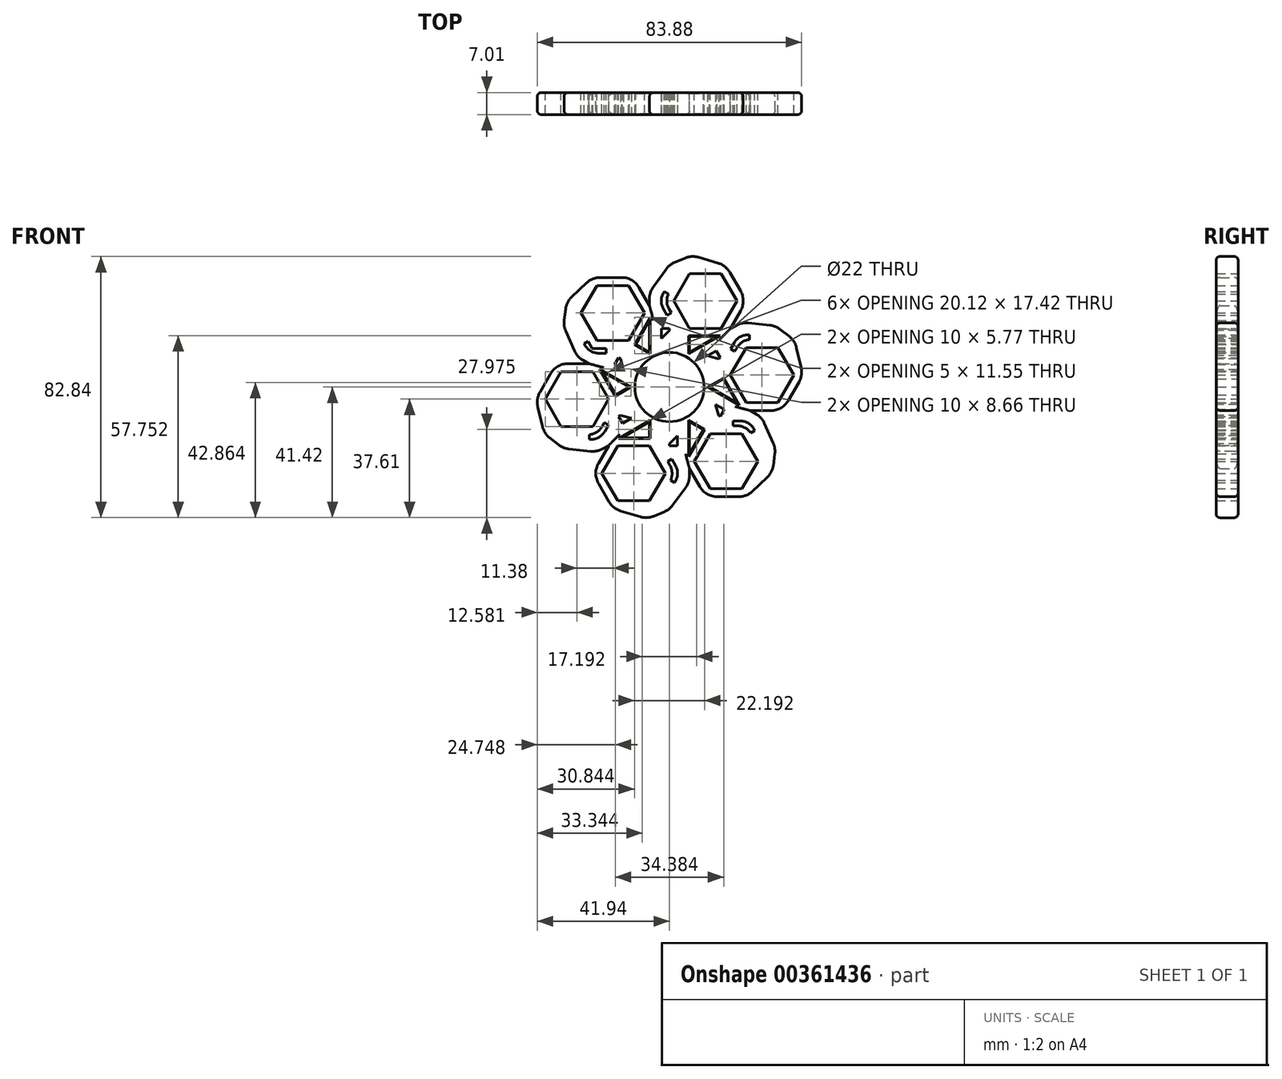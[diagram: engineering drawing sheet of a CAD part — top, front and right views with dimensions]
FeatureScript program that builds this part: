
annotation { "Feature Type Name" : "Feature", "Feature Type Description" : "" }
export const myFeature = defineFeature(function(context is Context, id is Id, definition is map)
    precondition{}
    {
        {
            var Q0;
            Q0=qCreatedBy(makeId("Front.planeOp"),FACE);
            var sketch = newSketch(context, id + "F0", { "sketchPlane" : qUnion([Q0])});
            skCircle(sketch, "E0.cCircle", {"center": v(0, 0) * mm, "radius": 11 * mm, "construction": true});
            skLineSegment(sketch, "E0.0", {"start": v(6.35, -11) * mm, "end": v(-6.35, -11) * mm});
            skLineSegment(sketch, "E0.1", {"start": v(-6.35, -11) * mm, "end": v(-12.7, 0) * mm});
            skLineSegment(sketch, "E0.2", {"start": v(-12.7, 0) * mm, "end": v(-6.35, 11) * mm});
            skLineSegment(sketch, "E0.3", {"start": v(-6.35, 11) * mm, "end": v(6.35, 11) * mm});
            skLineSegment(sketch, "E0.4", {"start": v(6.35, 11) * mm, "end": v(12.7, 0) * mm});
            skLineSegment(sketch, "E0.5", {"start": v(12.7, 0) * mm, "end": v(6.35, -11) * mm});
            skPoint(sketch, "E0.0.midPoint", {"position": v(0, -11) * mm});
            skCircle(sketch, "E1.cCircle", {"center": v(11.38, 27.33) * mm, "radius": 8.71 * mm, "construction": true});
            skLineSegment(sketch, "E1.0", {"start": v(16.4, 18.62) * mm, "end": v(6.35, 18.62) * mm});
            skLineSegment(sketch, "E1.1", {"start": v(6.35, 18.62) * mm, "end": v(1.32, 27.33) * mm});
            skLineSegment(sketch, "E1.2", {"start": v(1.32, 27.33) * mm, "end": v(6.35, 36.04) * mm});
            skLineSegment(sketch, "E1.3", {"start": v(6.35, 36.04) * mm, "end": v(16.4, 36.04) * mm});
            skLineSegment(sketch, "E1.4", {"start": v(16.4, 36.04) * mm, "end": v(21.44, 27.33) * mm});
            skLineSegment(sketch, "E1.5", {"start": v(21.44, 27.33) * mm, "end": v(16.4, 18.62) * mm});
            skPoint(sketch, "E1.0.midPoint", {"position": v(11.38, 18.62) * mm});
            skLineSegment(sketch, "E2", {"start": v(6.35, 11) * mm, "end": v(6.35, 18.62) * mm});
            skLineSegment(sketch, "E3", {"start": v(-6.35, 11) * mm, "end": v(-6.35, 30.15) * mm});
            skLineSegment(sketch, "E4", {"start": v(0, 38.86) * mm, "end": v(-6.35, 30.15) * mm});
            skLineSegment(sketch, "E5", {"start": v(7.1, 41.8) * mm, "end": v(0, 38.86) * mm});
            skLineSegment(sketch, "E6.0", {"start": v(-1.61, 27.33) * mm, "end": v(4.88, 38.58) * mm});
            skLineSegment(sketch, "E6.1", {"start": v(17.88, 38.58) * mm, "end": v(24.37, 27.33) * mm});
            skLineSegment(sketch, "E6.2", {"start": v(24.37, 27.33) * mm, "end": v(17.88, 16.08) * mm});
            skLineSegment(sketch, "E6.3", {"start": v(4.88, 38.58) * mm, "end": v(17.88, 38.58) * mm});
            skLineSegment(sketch, "E6.4", {"start": v(17.88, 16.08) * mm, "end": v(4.88, 16.08) * mm});
            skLineSegment(sketch, "E6.5", {"start": v(4.88, 16.08) * mm, "end": v(-1.61, 27.33) * mm});
            skLineSegment(sketch, "E7", {"start": v(17.88, 38.58) * mm, "end": v(7.1, 41.8) * mm});
            skLineSegment(sketch, "E8.1.0", {"start": v(-32.65, 27.06) * mm, "end": v(-33.65, 19.43) * mm});
            skLineSegment(sketch, "E8.1.1", {"start": v(-24.48, 34.77) * mm, "end": v(-32.65, 27.06) * mm});
            skLineSegment(sketch, "E8.1.2", {"start": v(-24.48, 34.77) * mm, "end": v(-11.48, 34.77) * mm});
            skLineSegment(sketch, "E8.1.3", {"start": v(-11.48, 34.77) * mm, "end": v(-4.99, 23.52) * mm});
            skLineSegment(sketch, "E8.1.4", {"start": v(-4.99, 23.52) * mm, "end": v(-11.48, 12.27) * mm});
            skLineSegment(sketch, "E8.1.5", {"start": v(-11.48, 12.27) * mm, "end": v(-24.48, 12.27) * mm});
            skLineSegment(sketch, "E8.1.6", {"start": v(-24.48, 12.27) * mm, "end": v(-30.97, 23.52) * mm});
            skLineSegment(sketch, "E8.1.7", {"start": v(-23, 14.8) * mm, "end": v(-28.04, 23.52) * mm});
            skCircle(sketch, "E8.1.8", {"center": v(-17.98, 23.52) * mm, "radius": 8.71 * mm, "construction": true});
            skLineSegment(sketch, "E8.1.9", {"start": v(-33.65, 19.43) * mm, "end": v(-29.28, 9.57) * mm});
            skLineSegment(sketch, "E8.1.10", {"start": v(-23, 32.23) * mm, "end": v(-12.95, 32.23) * mm});
            skLineSegment(sketch, "E8.1.11", {"start": v(-12.7, 0) * mm, "end": v(-29.28, 9.57) * mm});
            skPoint(sketch, "E8.1.12", {"position": v(-10.43, 19.16) * mm});
            skLineSegment(sketch, "E8.1.13", {"start": v(-12.95, 32.23) * mm, "end": v(-7.92, 23.52) * mm});
            skLineSegment(sketch, "E8.1.14", {"start": v(-30.97, 23.52) * mm, "end": v(-24.48, 34.77) * mm});
            skLineSegment(sketch, "E8.1.15", {"start": v(-12.95, 14.8) * mm, "end": v(-23, 14.8) * mm});
            skLineSegment(sketch, "E8.1.16", {"start": v(-7.92, 23.52) * mm, "end": v(-12.95, 14.8) * mm});
            skLineSegment(sketch, "E8.1.17", {"start": v(-28.04, 23.52) * mm, "end": v(-23, 32.23) * mm});
            skLineSegment(sketch, "E8.1.18", {"start": v(-6.35, 11) * mm, "end": v(-12.95, 14.8) * mm});
            skLineSegment(sketch, "E8.2.0", {"start": v(-39.76, -14.75) * mm, "end": v(-33.65, -19.43) * mm});
            skLineSegment(sketch, "E8.2.1", {"start": v(-42.35, -3.81) * mm, "end": v(-39.76, -14.75) * mm});
            skLineSegment(sketch, "E8.2.2", {"start": v(-42.35, -3.8) * mm, "end": v(-35.86, 7.44) * mm});
            skLineSegment(sketch, "E8.2.3", {"start": v(-35.86, 7.44) * mm, "end": v(-22.86, 7.44) * mm});
            skLineSegment(sketch, "E8.2.4", {"start": v(-22.86, 7.44) * mm, "end": v(-16.37, -3.81) * mm});
            skLineSegment(sketch, "E8.2.5", {"start": v(-16.37, -3.8) * mm, "end": v(-22.86, -15.06) * mm});
            skLineSegment(sketch, "E8.2.6", {"start": v(-22.86, -15.06) * mm, "end": v(-35.86, -15.06) * mm});
            skLineSegment(sketch, "E8.2.7", {"start": v(-24.33, -12.52) * mm, "end": v(-34.39, -12.52) * mm});
            skCircle(sketch, "E8.2.8", {"center": v(-29.36, -3.81) * mm, "radius": 8.71 * mm, "construction": true});
            skLineSegment(sketch, "E8.2.9", {"start": v(-33.65, -19.43) * mm, "end": v(-22.93, -20.57) * mm});
            skLineSegment(sketch, "E8.2.10", {"start": v(-39.42, -3.81) * mm, "end": v(-34.39, 4.9) * mm});
            skLineSegment(sketch, "E8.2.11", {"start": v(-6.35, -11) * mm, "end": v(-22.93, -20.57) * mm});
            skPoint(sketch, "E8.2.12", {"position": v(-21.81, 0.55) * mm});
            skLineSegment(sketch, "E8.2.13", {"start": v(-34.39, 4.9) * mm, "end": v(-24.33, 4.9) * mm});
            skLineSegment(sketch, "E8.2.14", {"start": v(-35.86, -15.06) * mm, "end": v(-42.35, -3.81) * mm});
            skLineSegment(sketch, "E8.2.15", {"start": v(-19.3, -3.81) * mm, "end": v(-24.33, -12.52) * mm});
            skLineSegment(sketch, "E8.2.16", {"start": v(-24.33, 4.9) * mm, "end": v(-19.3, -3.81) * mm});
            skLineSegment(sketch, "E8.2.17", {"start": v(-34.39, -12.52) * mm, "end": v(-39.42, -3.81) * mm});
            skLineSegment(sketch, "E8.2.18", {"start": v(-12.7, 0) * mm, "end": v(-19.3, -3.81) * mm});
            skLineSegment(sketch, "E9.2.3.0", {"start": v(-7.1, -41.8) * mm, "end": v(0, -38.86) * mm});
            skLineSegment(sketch, "E9.3.3.0", {"start": v(-17.88, -38.58) * mm, "end": v(-7.1, -41.8) * mm});
            skLineSegment(sketch, "E9.6.3.0", {"start": v(-17.88, -38.58) * mm, "end": v(-24.37, -27.33) * mm});
            skLineSegment(sketch, "E9.9.3.0", {"start": v(-24.37, -27.33) * mm, "end": v(-17.88, -16.08) * mm});
            skLineSegment(sketch, "E9.12.3.0", {"start": v(-17.88, -16.08) * mm, "end": v(-4.88, -16.08) * mm});
            skLineSegment(sketch, "E9.15.3.0", {"start": v(-4.88, -16.08) * mm, "end": v(1.61, -27.33) * mm});
            skLineSegment(sketch, "E9.18.3.0", {"start": v(1.61, -27.33) * mm, "end": v(-4.88, -38.58) * mm});
            skLineSegment(sketch, "E9.21.3.0", {"start": v(-1.32, -27.33) * mm, "end": v(-6.35, -36.04) * mm});
            skCircle(sketch, "E9.24.3.0", {"center": v(-11.38, -27.33) * mm, "radius": 8.71 * mm, "construction": true});
            skLineSegment(sketch, "E9.26.3.0", {"start": v(0, -38.86) * mm, "end": v(6.35, -30.15) * mm});
            skLineSegment(sketch, "E9.29.3.0", {"start": v(-16.4, -36.04) * mm, "end": v(-21.44, -27.33) * mm});
            skLineSegment(sketch, "E9.32.3.0", {"start": v(6.35, -11) * mm, "end": v(6.35, -30.15) * mm});
            skPoint(sketch, "E9.35.3.0", {"position": v(-11.38, -18.62) * mm});
            skLineSegment(sketch, "E9.36.3.0", {"start": v(-21.44, -27.33) * mm, "end": v(-16.4, -18.62) * mm});
            skLineSegment(sketch, "E9.39.3.0", {"start": v(-4.88, -38.58) * mm, "end": v(-17.88, -38.58) * mm});
            skLineSegment(sketch, "E9.42.3.0", {"start": v(-6.35, -18.62) * mm, "end": v(-1.32, -27.33) * mm});
            skLineSegment(sketch, "E9.45.3.0", {"start": v(-16.4, -18.62) * mm, "end": v(-6.35, -18.62) * mm});
            skLineSegment(sketch, "E9.48.3.0", {"start": v(-6.35, -36.04) * mm, "end": v(-16.4, -36.04) * mm});
            skLineSegment(sketch, "E9.51.3.0", {"start": v(-6.35, -11) * mm, "end": v(-6.35, -18.62) * mm});
            skLineSegment(sketch, "E9.2.4.0", {"start": v(32.65, -27.06) * mm, "end": v(33.65, -19.43) * mm});
            skLineSegment(sketch, "E9.3.4.0", {"start": v(24.48, -34.77) * mm, "end": v(32.65, -27.06) * mm});
            skLineSegment(sketch, "E9.6.4.0", {"start": v(24.48, -34.77) * mm, "end": v(11.48, -34.77) * mm});
            skLineSegment(sketch, "E9.9.4.0", {"start": v(11.48, -34.77) * mm, "end": v(4.99, -23.52) * mm});
            skLineSegment(sketch, "E9.12.4.0", {"start": v(4.99, -23.52) * mm, "end": v(11.48, -12.27) * mm});
            skLineSegment(sketch, "E9.15.4.0", {"start": v(11.48, -12.27) * mm, "end": v(24.48, -12.27) * mm});
            skLineSegment(sketch, "E9.18.4.0", {"start": v(24.48, -12.27) * mm, "end": v(30.97, -23.52) * mm});
            skLineSegment(sketch, "E9.21.4.0", {"start": v(23, -14.8) * mm, "end": v(28.04, -23.52) * mm});
            skCircle(sketch, "E9.24.4.0", {"center": v(17.98, -23.52) * mm, "radius": 8.71 * mm, "construction": true});
            skLineSegment(sketch, "E9.26.4.0", {"start": v(33.65, -19.43) * mm, "end": v(29.28, -9.57) * mm});
            skLineSegment(sketch, "E9.29.4.0", {"start": v(23, -32.23) * mm, "end": v(12.95, -32.23) * mm});
            skLineSegment(sketch, "E9.32.4.0", {"start": v(12.7, 0) * mm, "end": v(29.28, -9.57) * mm});
            skPoint(sketch, "E9.35.4.0", {"position": v(10.43, -19.16) * mm});
            skLineSegment(sketch, "E9.36.4.0", {"start": v(12.95, -32.23) * mm, "end": v(7.92, -23.52) * mm});
            skLineSegment(sketch, "E9.39.4.0", {"start": v(30.97, -23.52) * mm, "end": v(24.48, -34.77) * mm});
            skLineSegment(sketch, "E9.42.4.0", {"start": v(12.95, -14.8) * mm, "end": v(23, -14.8) * mm});
            skLineSegment(sketch, "E9.45.4.0", {"start": v(7.92, -23.52) * mm, "end": v(12.95, -14.8) * mm});
            skLineSegment(sketch, "E9.48.4.0", {"start": v(28.04, -23.52) * mm, "end": v(23, -32.23) * mm});
            skLineSegment(sketch, "E9.51.4.0", {"start": v(6.35, -11) * mm, "end": v(12.95, -14.8) * mm});
            skLineSegment(sketch, "E9.2.5.0", {"start": v(39.76, 14.75) * mm, "end": v(33.65, 19.43) * mm});
            skLineSegment(sketch, "E9.3.5.0", {"start": v(42.35, 3.81) * mm, "end": v(39.76, 14.75) * mm});
            skLineSegment(sketch, "E9.6.5.0", {"start": v(42.35, 3.81) * mm, "end": v(35.86, -7.44) * mm});
            skLineSegment(sketch, "E9.9.5.0", {"start": v(35.86, -7.44) * mm, "end": v(22.86, -7.44) * mm});
            skLineSegment(sketch, "E9.12.5.0", {"start": v(22.86, -7.44) * mm, "end": v(16.37, 3.81) * mm});
            skLineSegment(sketch, "E9.15.5.0", {"start": v(16.37, 3.81) * mm, "end": v(22.86, 15.06) * mm});
            skLineSegment(sketch, "E9.18.5.0", {"start": v(22.86, 15.06) * mm, "end": v(35.86, 15.06) * mm});
            skLineSegment(sketch, "E9.21.5.0", {"start": v(24.33, 12.52) * mm, "end": v(34.39, 12.52) * mm});
            skCircle(sketch, "E9.24.5.0", {"center": v(29.36, 3.81) * mm, "radius": 8.71 * mm, "construction": true});
            skLineSegment(sketch, "E9.26.5.0", {"start": v(33.65, 19.43) * mm, "end": v(22.93, 20.57) * mm});
            skLineSegment(sketch, "E9.29.5.0", {"start": v(39.42, 3.8) * mm, "end": v(34.39, -4.9) * mm});
            skLineSegment(sketch, "E9.32.5.0", {"start": v(6.35, 11) * mm, "end": v(22.93, 20.57) * mm});
            skPoint(sketch, "E9.35.5.0", {"position": v(21.81, -0.55) * mm});
            skLineSegment(sketch, "E9.36.5.0", {"start": v(34.39, -4.9) * mm, "end": v(24.33, -4.9) * mm});
            skLineSegment(sketch, "E9.39.5.0", {"start": v(35.86, 15.06) * mm, "end": v(42.35, 3.81) * mm});
            skLineSegment(sketch, "E9.42.5.0", {"start": v(19.3, 3.81) * mm, "end": v(24.33, 12.52) * mm});
            skLineSegment(sketch, "E9.45.5.0", {"start": v(24.33, -4.9) * mm, "end": v(19.3, 3.81) * mm});
            skLineSegment(sketch, "E9.48.5.0", {"start": v(34.39, 12.52) * mm, "end": v(39.42, 3.81) * mm});
            skLineSegment(sketch, "E9.51.5.0", {"start": v(12.7, 0) * mm, "end": v(19.3, 3.81) * mm});
            skCircle(sketch, "E10", {"center": v(0, 0) * mm, "radius": 11 * mm});
            skLineSegment(sketch, "E11", {"start": v(0, 0) * mm, "end": v(0, 18.62) * mm});
            skLineSegment(sketch, "E12", {"start": v(0, 18.62) * mm, "end": v(-2.54, 18.62) * mm});
            skLineSegment(sketch, "E13", {"start": v(-2.54, 18.62) * mm, "end": v(-2.54, 13.54) * mm});
            skLineSegment(sketch, "E14", {"start": v(-2.54, 13.54) * mm, "end": v(0, 13.54) * mm});
            skPoint(sketch, "E14.endSnap0", {"position": v(0, 11) * mm});
            skLineSegment(sketch, "E15.1.0", {"start": v(-16.12, 9.3) * mm, "end": v(-17.4, 7.1) * mm});
            skLineSegment(sketch, "E15.1.1", {"start": v(-17.4, 7.1) * mm, "end": v(-13, 4.57) * mm});
            skLineSegment(sketch, "E15.1.2", {"start": v(-13, 4.57) * mm, "end": v(-11.72, 6.77) * mm});
            skLineSegment(sketch, "E15.1.3", {"start": v(0, 0) * mm, "end": v(-16.12, 9.3) * mm});
            skLineSegment(sketch, "E15.2.0", {"start": v(-16.12, -9.3) * mm, "end": v(-14.85, -11.5) * mm});
            skLineSegment(sketch, "E15.2.1", {"start": v(-14.85, -11.5) * mm, "end": v(-10.45, -8.97) * mm});
            skLineSegment(sketch, "E15.2.2", {"start": v(-10.45, -8.97) * mm, "end": v(-11.72, -6.77) * mm});
            skLineSegment(sketch, "E15.2.3", {"start": v(0, 0) * mm, "end": v(-16.12, -9.3) * mm});
            skLineSegment(sketch, "E16.2.3.0", {"start": v(0, -18.62) * mm, "end": v(2.54, -18.62) * mm});
            skLineSegment(sketch, "E16.3.3.0", {"start": v(2.54, -18.62) * mm, "end": v(2.54, -13.54) * mm});
            skLineSegment(sketch, "E16.6.3.0", {"start": v(2.54, -13.54) * mm, "end": v(0, -13.54) * mm});
            skLineSegment(sketch, "E16.9.3.0", {"start": v(0, 0) * mm, "end": v(0, -18.62) * mm});
            skLineSegment(sketch, "E16.2.4.0", {"start": v(16.12, -9.3) * mm, "end": v(17.4, -7.1) * mm});
            skLineSegment(sketch, "E16.3.4.0", {"start": v(17.4, -7.1) * mm, "end": v(13, -4.57) * mm});
            skLineSegment(sketch, "E16.6.4.0", {"start": v(13, -4.57) * mm, "end": v(11.72, -6.77) * mm});
            skLineSegment(sketch, "E16.9.4.0", {"start": v(0, 0) * mm, "end": v(16.12, -9.3) * mm});
            skLineSegment(sketch, "E16.2.5.0", {"start": v(16.12, 9.3) * mm, "end": v(14.85, 11.5) * mm});
            skLineSegment(sketch, "E16.3.5.0", {"start": v(14.85, 11.5) * mm, "end": v(10.45, 8.97) * mm});
            skLineSegment(sketch, "E16.6.5.0", {"start": v(10.45, 8.97) * mm, "end": v(11.72, 6.77) * mm});
            skLineSegment(sketch, "E16.9.5.0", {"start": v(0, 0) * mm, "end": v(16.12, 9.3) * mm});
            skLineSegment(sketch, "E17", {"start": v(-24.48, 12.27) * mm, "end": v(-25.76, 14.5) * mm});
            skPoint(sketch, "E17.endSnap0", {"position": v(-31.47, 14.5) * mm});
            skLineSegment(sketch, "E18", {"start": v(-24.48, 12.27) * mm, "end": v(-20.13, 12.27) * mm});
            skLineSegment(sketch, "E19.0", {"start": v(-25.36, 10.74) * mm, "end": v(-27.08, 13.74) * mm});
            skLineSegment(sketch, "E19.1", {"start": v(-25.36, 10.74) * mm, "end": v(-20.13, 10.74) * mm});
            skLineSegment(sketch, "E20", {"start": v(-27.08, 13.74) * mm, "end": v(-25.76, 14.5) * mm});
            skLineSegment(sketch, "E21", {"start": v(-20.13, 12.27) * mm, "end": v(-20.13, 10.74) * mm});
            skLineSegment(sketch, "E22.1.0", {"start": v(-25.44, -16.59) * mm, "end": v(-25.44, -15.06) * mm});
            skLineSegment(sketch, "E22.1.1", {"start": v(-21.98, -16.59) * mm, "end": v(-25.44, -16.59) * mm});
            skLineSegment(sketch, "E22.1.2", {"start": v(-21.98, -16.59) * mm, "end": v(-19.37, -12.06) * mm});
            skLineSegment(sketch, "E22.1.3", {"start": v(-20.7, -11.3) * mm, "end": v(-19.37, -12.06) * mm});
            skLineSegment(sketch, "E22.2.0", {"start": v(1.64, -30.33) * mm, "end": v(0.32, -29.56) * mm});
            skLineSegment(sketch, "E22.2.1", {"start": v(3.37, -27.33) * mm, "end": v(1.64, -30.33) * mm});
            skLineSegment(sketch, "E22.2.2", {"start": v(3.37, -27.33) * mm, "end": v(0.76, -22.8) * mm});
            skLineSegment(sketch, "E22.2.3", {"start": v(-0.56, -23.57) * mm, "end": v(0.76, -22.8) * mm});
            skLineSegment(sketch, "E23.3.3.0", {"start": v(25.36, -10.74) * mm, "end": v(27.08, -13.74) * mm});
            skLineSegment(sketch, "E23.4.3.0", {"start": v(27.08, -13.74) * mm, "end": v(25.76, -14.5) * mm});
            skLineSegment(sketch, "E23.6.3.0", {"start": v(25.36, -10.74) * mm, "end": v(20.13, -10.74) * mm});
            skLineSegment(sketch, "E23.9.3.0", {"start": v(20.13, -12.27) * mm, "end": v(20.13, -10.74) * mm});
            skLineSegment(sketch, "E23.3.4.0", {"start": v(21.98, 16.59) * mm, "end": v(25.44, 16.59) * mm});
            skLineSegment(sketch, "E23.4.4.0", {"start": v(25.44, 16.59) * mm, "end": v(25.44, 15.06) * mm});
            skLineSegment(sketch, "E23.6.4.0", {"start": v(21.98, 16.59) * mm, "end": v(19.37, 12.06) * mm});
            skLineSegment(sketch, "E23.9.4.0", {"start": v(20.7, 11.3) * mm, "end": v(19.37, 12.06) * mm});
            skLineSegment(sketch, "E23.3.5.0", {"start": v(-3.37, 27.33) * mm, "end": v(-1.64, 30.33) * mm});
            skLineSegment(sketch, "E23.4.5.0", {"start": v(-1.64, 30.33) * mm, "end": v(-0.32, 29.56) * mm});
            skLineSegment(sketch, "E23.6.5.0", {"start": v(-3.37, 27.33) * mm, "end": v(-0.76, 22.8) * mm});
            skLineSegment(sketch, "E23.9.5.0", {"start": v(0.56, 23.57) * mm, "end": v(-0.76, 22.8) * mm});
            skSolve(sketch);
        }
        {
            var Q0;
            {var subQ5=sQuery(id+"F0.wireOp",EDGE,"E0.3");Q0=makeQuery(id+"F0.imprint","IMPRINT",FACE,{"disambiguationData":[TD([[makeQuery(id+"F0.imprint","IMPRINT",EDGE,{"derivedFrom":subQ5}),1.0]])]});}
            var Q1;
            Q1=makeQuery(id+"F0.imprint","IMPRINT",FACE,{"disambiguationData":[TD([[makeQuery(id+"F0.imprint","IMPRINT",EDGE,{"derivedFrom":sQuery(id+"F0.wireOp",EDGE,"E0.0")}),-1.0]])]});
            var Q2;
            {var subQ3=sQuery(id+"F0.wireOp",EDGE,"E8.2.2");Q2=makeQuery(id+"F0.imprint","IMPRINT",FACE,{"disambiguationData":[TD([[makeQuery(id+"F0.imprint","IMPRINT",EDGE,{"derivedFrom":subQ3}),-1.0]])]});}
            var Q3;
            {var subQ7=sQuery(id+"F0.wireOp",EDGE,"E8.1.2");Q3=makeQuery(id+"F0.imprint","IMPRINT",FACE,{"disambiguationData":[TD([[makeQuery(id+"F0.imprint","IMPRINT",EDGE,{"derivedFrom":subQ7}),-1.0]])]});}
            var Q4;
            Q4=makeQuery(id+"F0.imprint","IMPRINT",FACE,{"disambiguationData":[TD([[makeQuery(id+"F0.imprint","IMPRINT",EDGE,{"derivedFrom":sQuery(id+"F0.wireOp",EDGE,"E1.0")}),1.0]])]});
            var Q5;
            {var subQ3=sQuery(id+"F0.wireOp",EDGE,"E9.6.5.0");Q5=makeQuery(id+"F0.imprint","IMPRINT",FACE,{"disambiguationData":[TD([[makeQuery(id+"F0.imprint","IMPRINT",EDGE,{"derivedFrom":subQ3}),-1.0]])]});}
            var Q6;
            {var subQ3=sQuery(id+"F0.wireOp",EDGE,"E9.6.4.0");Q6=makeQuery(id+"F0.imprint","IMPRINT",FACE,{"disambiguationData":[TD([[makeQuery(id+"F0.imprint","IMPRINT",EDGE,{"derivedFrom":subQ3}),-1.0]])]});}
            var Q7;
            {var subQ3=sQuery(id+"F0.wireOp",EDGE,"E9.6.3.0");Q7=makeQuery(id+"F0.imprint","IMPRINT",FACE,{"disambiguationData":[TD([[makeQuery(id+"F0.imprint","IMPRINT",EDGE,{"derivedFrom":subQ3}),-1.0]])]});}
            var Q8;
            {var subQ0=sQuery(id+"F0.wireOp",EDGE,"E8.2.3");var subQ1=sQuery(id+"F0.wireOp",EDGE,"E8.1.11");var subQ2=makeQuery(id+"F0.imprint","INTERSECT",VERTEX,{"derivedFrom":[subQ1,subQ0]});Q8=makeQuery(id+"F0.imprint","IMPRINT",FACE,{"disambiguationData":[TD([[makeQuery(id+"F0.imprint","IMPRINT",EDGE,{"disambiguationData":[TD([[subQ2,1.0]])],"derivedFrom":subQ1}),-1.0]])]});}
            var Q9;
            {var subQ0=sQuery(id+"F0.wireOp",EDGE,"E6.4");var subQ1=sQuery(id+"F0.wireOp",EDGE,"E6.2");var subQ2=makeQuery(id+"F0.imprint","INTERSECT",VERTEX,{"derivedFrom":[subQ1,subQ0]});Q9=makeQuery(id+"F0.imprint","IMPRINT",FACE,{"disambiguationData":[TD([[makeQuery(id+"F0.imprint","IMPRINT",EDGE,{"disambiguationData":[TD([[subQ2,1.0]])],"derivedFrom":subQ1}),-1.0]])]});}
            var Q10;
            {var subQ0=sQuery(id+"F0.wireOp",EDGE,"E9.9.5.0");var subQ1=sQuery(id+"F0.wireOp",EDGE,"E9.32.4.0");var subQ2=makeQuery(id+"F0.imprint","INTERSECT",VERTEX,{"derivedFrom":[subQ1,subQ0]});Q10=makeQuery(id+"F0.imprint","IMPRINT",FACE,{"disambiguationData":[TD([[makeQuery(id+"F0.imprint","IMPRINT",EDGE,{"disambiguationData":[TD([[subQ2,1.0]])],"derivedFrom":subQ1}),-1.0]])]});}
            var Q11;
            {var subQ0=sQuery(id+"F0.wireOp",EDGE,"E9.9.4.0");var subQ1=sQuery(id+"F0.wireOp",EDGE,"E9.32.3.0");var subQ2=makeQuery(id+"F0.imprint","INTERSECT",VERTEX,{"derivedFrom":[subQ1,subQ0]});Q11=makeQuery(id+"F0.imprint","IMPRINT",FACE,{"disambiguationData":[TD([[makeQuery(id+"F0.imprint","IMPRINT",EDGE,{"disambiguationData":[TD([[subQ2,1.0]])],"derivedFrom":subQ1}),-1.0]])]});}
            var Q12;
            {var subQ0=sQuery(id+"F0.wireOp",EDGE,"E9.9.3.0");var subQ1=sQuery(id+"F0.wireOp",EDGE,"E8.2.11");var subQ2=makeQuery(id+"F0.imprint","INTERSECT",VERTEX,{"derivedFrom":[subQ1,subQ0]});Q12=makeQuery(id+"F0.imprint","IMPRINT",FACE,{"disambiguationData":[TD([[makeQuery(id+"F0.imprint","IMPRINT",EDGE,{"disambiguationData":[TD([[subQ2,1.0]])],"derivedFrom":subQ1}),-1.0]])]});}
            var Q13;
            {var subQ0=sQuery(id+"F0.wireOp",EDGE,"E8.1.3");var subQ1=sQuery(id+"F0.wireOp",EDGE,"E3");var subQ2=makeQuery(id+"F0.imprint","INTERSECT",VERTEX,{"derivedFrom":[subQ1,subQ0]});Q13=makeQuery(id+"F0.imprint","IMPRINT",FACE,{"disambiguationData":[TD([[makeQuery(id+"F0.imprint","IMPRINT",EDGE,{"disambiguationData":[TD([[subQ2,1.0]])],"derivedFrom":subQ1}),-1.0]])]});}
            var Q14;
            {var subQ1=sQuery(id+"F0.wireOp",EDGE,"E0.2");var subQ3=sQuery(id+"F0.wireOp",EDGE,"E10");var subQ4=makeQuery(id+"F0.imprint","INTERSECT",VERTEX,{"derivedFrom":[subQ1,subQ3]});Q14=makeQuery(id+"F0.imprint","IMPRINT",FACE,{"disambiguationData":[TD([[makeQuery(id+"F0.imprint","IMPRINT",EDGE,{"disambiguationData":[TD([[subQ4,1.0]])],"derivedFrom":subQ3}),-1.0]])]});}
            var Q15;
            {var subQ1=sQuery(id+"F0.wireOp",EDGE,"E0.1");var subQ3=sQuery(id+"F0.wireOp",EDGE,"E10");var subQ4=makeQuery(id+"F0.imprint","INTERSECT",VERTEX,{"derivedFrom":[subQ1,subQ3]});Q15=makeQuery(id+"F0.imprint","IMPRINT",FACE,{"disambiguationData":[TD([[makeQuery(id+"F0.imprint","IMPRINT",EDGE,{"disambiguationData":[TD([[subQ4,1.0]])],"derivedFrom":subQ3}),-1.0]])]});}
            var Q16;
            {var subQ1=sQuery(id+"F0.wireOp",EDGE,"E0.4");var subQ3=sQuery(id+"F0.wireOp",EDGE,"E10");var subQ4=makeQuery(id+"F0.imprint","INTERSECT",VERTEX,{"derivedFrom":[subQ1,subQ3]});Q16=makeQuery(id+"F0.imprint","IMPRINT",FACE,{"disambiguationData":[TD([[makeQuery(id+"F0.imprint","IMPRINT",EDGE,{"disambiguationData":[TD([[subQ4,1.0]])],"derivedFrom":subQ3}),-1.0]])]});}
            var Q17;
            {var subQ1=sQuery(id+"F0.wireOp",EDGE,"E0.3");var subQ3=sQuery(id+"F0.wireOp",EDGE,"E10");var subQ4=makeQuery(id+"F0.imprint","INTERSECT",VERTEX,{"derivedFrom":[subQ1,subQ3]});Q17=makeQuery(id+"F0.imprint","IMPRINT",FACE,{"disambiguationData":[TD([[makeQuery(id+"F0.imprint","IMPRINT",EDGE,{"disambiguationData":[TD([[subQ4,1.0]])],"derivedFrom":subQ3}),-1.0]])]});}
            var Q18;
            Q18=makeQuery(id+"F0.imprint","IMPRINT",FACE,{"disambiguationData":[TD([[makeQuery(id+"F0.imprint","IMPRINT",EDGE,{"derivedFrom":sQuery(id+"F0.wireOp",EDGE,"E8.1.0")}),1.0]])]});
            var Q19;
            Q19=makeQuery(id+"F0.imprint","IMPRINT",FACE,{"disambiguationData":[TD([[makeQuery(id+"F0.imprint","IMPRINT",EDGE,{"derivedFrom":sQuery(id+"F0.wireOp",EDGE,"E9.2.5.0")}),1.0]])]});
            var Q20;
            Q20=makeQuery(id+"F0.imprint","IMPRINT",FACE,{"disambiguationData":[TD([[makeQuery(id+"F0.imprint","IMPRINT",EDGE,{"derivedFrom":sQuery(id+"F0.wireOp",EDGE,"E9.2.4.0")}),1.0]])]});
            var Q21;
            Q21=makeQuery(id+"F0.imprint","IMPRINT",FACE,{"disambiguationData":[TD([[makeQuery(id+"F0.imprint","IMPRINT",EDGE,{"derivedFrom":sQuery(id+"F0.wireOp",EDGE,"E9.2.3.0")}),1.0]])]});
            var Q22;
            Q22=makeQuery(id+"F0.imprint","IMPRINT",FACE,{"disambiguationData":[TD([[makeQuery(id+"F0.imprint","IMPRINT",EDGE,{"derivedFrom":sQuery(id+"F0.wireOp",EDGE,"E8.2.0")}),1.0]])]});
            var Q23;
            {var subQ0=sQuery(id+"F0.wireOp",EDGE,"fc4139a8-f376-4695-9052-6e1d18b9356a0.MirrorCS");Q23=makeQuery(id+"F0.imprint","IMPRINT",FACE,{"disambiguationData":[TD([[makeQuery(id+"F0.imprint","IMPRINT",EDGE,{"derivedFrom":subQ0}),-1.0]])]});}
            var Q24;
            {var subQ0=sQuery(id+"F0.wireOp",EDGE,"5a5fe9bc-91fb-4634-9269-3f49f482236a.1.0");Q24=makeQuery(id+"F0.imprint","IMPRINT",FACE,{"disambiguationData":[TD([[makeQuery(id+"F0.imprint","IMPRINT",EDGE,{"derivedFrom":subQ0}),1.0]])]});}
            var Q25;
            {var subQ0=sQuery(id+"F0.wireOp",EDGE,"5a5fe9bc-91fb-4634-9269-3f49f482236a.2.0");Q25=makeQuery(id+"F0.imprint","IMPRINT",FACE,{"disambiguationData":[TD([[makeQuery(id+"F0.imprint","IMPRINT",EDGE,{"derivedFrom":subQ0}),1.0]])]});}
            var Q26;
            {var subQ0=sQuery(id+"F0.wireOp",EDGE,"14cd757c-f4b4-469d-932e-72476608e488.2.3.0");Q26=makeQuery(id+"F0.imprint","IMPRINT",FACE,{"disambiguationData":[TD([[makeQuery(id+"F0.imprint","IMPRINT",EDGE,{"derivedFrom":subQ0}),1.0]])]});}
            var Q27;
            {var subQ0=sQuery(id+"F0.wireOp",EDGE,"14cd757c-f4b4-469d-932e-72476608e488.2.4.0");Q27=makeQuery(id+"F0.imprint","IMPRINT",FACE,{"disambiguationData":[TD([[makeQuery(id+"F0.imprint","IMPRINT",EDGE,{"derivedFrom":subQ0}),1.0]])]});}
            var Q28;
            {var subQ0=sQuery(id+"F0.wireOp",EDGE,"14cd757c-f4b4-469d-932e-72476608e488.2.5.0");Q28=makeQuery(id+"F0.imprint","IMPRINT",FACE,{"disambiguationData":[TD([[makeQuery(id+"F0.imprint","IMPRINT",EDGE,{"derivedFrom":subQ0}),1.0]])]});}
            extrude(context, id + "F1", {"entities" : qUnion([Q0, Q1, Q2, Q3, Q4, Q5, Q6, Q7, Q8, Q9, Q10, Q11, Q12, Q13, Q14, Q15, Q16, Q17, Q18, Q19, Q20, Q21, Q22, Q23, Q24, Q25, Q26, Q27, Q28]), "depth" : 7 * mm, "offsetDistance" : 25.4 * mm});
        }
        {
            var Q0;
            Q0=makeQuery(id+"F1.opExtrude","CAP_EDGE",EDGE,{"disambiguationData":[OSD([sQuery(id+"F0.wireOp",EDGE,"E9.6.3.0")])],"isStart":false});
            var Q1;
            Q1=makeQuery(id+"F1.opExtrude","CAP_EDGE",EDGE,{"disambiguationData":[OSD([sQuery(id+"F0.wireOp",EDGE,"E9.3.3.0")])],"isStart":false});
            var Q2;
            Q2=makeQuery(id+"F1.opExtrude","CAP_EDGE",EDGE,{"disambiguationData":[OSD([sQuery(id+"F0.wireOp",EDGE,"E9.9.3.0")])],"isStart":false});
            var Q3;
            Q3=makeQuery(id+"F1.opExtrude","CAP_EDGE",EDGE,{"disambiguationData":[OSD([sQuery(id+"F0.wireOp",EDGE,"E9.2.3.0")])],"isStart":false});
            var Q4;
            Q4=makeQuery(id+"F1.opExtrude","CAP_EDGE",EDGE,{"disambiguationData":[OSD([sQuery(id+"F0.wireOp",EDGE,"E9.26.3.0")])],"isStart":false});
            var Q5;
            Q5=makeQuery(id+"F1.opExtrude","CAP_EDGE",EDGE,{"disambiguationData":[OSD([sQuery(id+"F0.wireOp",EDGE,"E9.9.4.0")])],"isStart":false});
            var Q6;
            {var subQ0=sQuery(id+"F0.wireOp",EDGE,"E9.32.3.0");Q6=makeQuery(id+"F1.opExtrude","CAP_EDGE",EDGE,{"disambiguationData":[OSD([subQ0]),TDD([makeQuery(id+"F0.imprint","IMPRINT",EDGE,{"disambiguationData":[TD([[makeQuery(id+"F0.imprint","INTERSECT",VERTEX,{"derivedFrom":[sQuery(id+"F0.wireOp",EDGE,"E9.26.3.0"),subQ0]}),1.0]])],"derivedFrom":subQ0})])],"isStart":false});}
            var Q7;
            {var subQ0=sQuery(id+"F0.wireOp",EDGE,"E8.2.11");Q7=makeQuery(id+"F1.opExtrude","CAP_EDGE",EDGE,{"disambiguationData":[OSD([subQ0]),TDD([makeQuery(id+"F0.imprint","IMPRINT",EDGE,{"disambiguationData":[TD([[makeQuery(id+"F0.imprint","INTERSECT",VERTEX,{"derivedFrom":[sQuery(id+"F0.wireOp",EDGE,"E8.2.9"),subQ0]}),1.0]])],"derivedFrom":subQ0})])],"isStart":false});}
            var Q8;
            Q8=makeQuery(id+"F1.opExtrude","CAP_EDGE",EDGE,{"disambiguationData":[OSD([sQuery(id+"F0.wireOp",EDGE,"E8.2.9")])],"isStart":false});
            var Q9;
            Q9=makeQuery(id+"F1.opExtrude","CAP_EDGE",EDGE,{"disambiguationData":[OSD([sQuery(id+"F0.wireOp",EDGE,"E9.6.4.0")])],"isStart":false});
            var Q10;
            Q10=makeQuery(id+"F1.opExtrude","CAP_EDGE",EDGE,{"disambiguationData":[OSD([sQuery(id+"F0.wireOp",EDGE,"E9.3.4.0")])],"isStart":false});
            var Q11;
            Q11=makeQuery(id+"F1.opExtrude","CAP_EDGE",EDGE,{"disambiguationData":[OSD([sQuery(id+"F0.wireOp",EDGE,"E9.2.4.0")])],"isStart":false});
            var Q12;
            Q12=makeQuery(id+"F1.opExtrude","CAP_EDGE",EDGE,{"disambiguationData":[OSD([sQuery(id+"F0.wireOp",EDGE,"E9.26.4.0")])],"isStart":false});
            var Q13;
            {var subQ0=sQuery(id+"F0.wireOp",EDGE,"E9.32.4.0");Q13=makeQuery(id+"F1.opExtrude","CAP_EDGE",EDGE,{"disambiguationData":[OSD([subQ0]),TDD([makeQuery(id+"F0.imprint","IMPRINT",EDGE,{"disambiguationData":[TD([[makeQuery(id+"F0.imprint","INTERSECT",VERTEX,{"derivedFrom":[sQuery(id+"F0.wireOp",EDGE,"E9.26.4.0"),subQ0]}),1.0]])],"derivedFrom":subQ0})])],"isStart":false});}
            var Q14;
            Q14=makeQuery(id+"F1.opExtrude","CAP_EDGE",EDGE,{"disambiguationData":[OSD([sQuery(id+"F0.wireOp",EDGE,"E9.9.5.0")])],"isStart":false});
            var Q15;
            Q15=makeQuery(id+"F1.opExtrude","CAP_EDGE",EDGE,{"disambiguationData":[OSD([sQuery(id+"F0.wireOp",EDGE,"E9.6.5.0")])],"isStart":false});
            var Q16;
            Q16=makeQuery(id+"F1.opExtrude","CAP_EDGE",EDGE,{"disambiguationData":[OSD([sQuery(id+"F0.wireOp",EDGE,"E9.3.5.0")])],"isStart":false});
            var Q17;
            Q17=makeQuery(id+"F1.opExtrude","CAP_EDGE",EDGE,{"disambiguationData":[OSD([sQuery(id+"F0.wireOp",EDGE,"E9.2.5.0")])],"isStart":false});
            var Q18;
            Q18=makeQuery(id+"F1.opExtrude","CAP_EDGE",EDGE,{"disambiguationData":[OSD([sQuery(id+"F0.wireOp",EDGE,"E9.26.5.0")])],"isStart":false});
            var Q19;
            {var subQ0=sQuery(id+"F0.wireOp",EDGE,"E9.32.5.0");Q19=makeQuery(id+"F1.opExtrude","CAP_EDGE",EDGE,{"disambiguationData":[OSD([subQ0]),TDD([makeQuery(id+"F0.imprint","IMPRINT",EDGE,{"disambiguationData":[TD([[makeQuery(id+"F0.imprint","INTERSECT",VERTEX,{"derivedFrom":[sQuery(id+"F0.wireOp",EDGE,"E9.26.5.0"),subQ0]}),1.0]])],"derivedFrom":subQ0})])],"isStart":false});}
            var Q20;
            Q20=makeQuery(id+"F1.opExtrude","CAP_EDGE",EDGE,{"disambiguationData":[OSD([sQuery(id+"F0.wireOp",EDGE,"E6.2")])],"isStart":false});
            var Q21;
            Q21=makeQuery(id+"F1.opExtrude","CAP_EDGE",EDGE,{"disambiguationData":[OSD([sQuery(id+"F0.wireOp",EDGE,"E6.1")])],"isStart":false});
            var Q22;
            Q22=makeQuery(id+"F1.opExtrude","CAP_EDGE",EDGE,{"disambiguationData":[OSD([sQuery(id+"F0.wireOp",EDGE,"E7")])],"isStart":false});
            var Q23;
            Q23=makeQuery(id+"F1.opExtrude","CAP_EDGE",EDGE,{"disambiguationData":[OSD([sQuery(id+"F0.wireOp",EDGE,"E5")])],"isStart":false});
            var Q24;
            Q24=makeQuery(id+"F1.opExtrude","CAP_EDGE",EDGE,{"disambiguationData":[OSD([sQuery(id+"F0.wireOp",EDGE,"E4")])],"isStart":false});
            var Q25;
            {var subQ0=sQuery(id+"F0.wireOp",EDGE,"E3");Q25=makeQuery(id+"F1.opExtrude","CAP_EDGE",EDGE,{"disambiguationData":[OSD([subQ0]),TDD([makeQuery(id+"F0.imprint","IMPRINT",EDGE,{"disambiguationData":[TD([[makeQuery(id+"F0.imprint","INTERSECT",VERTEX,{"derivedFrom":[subQ0,sQuery(id+"F0.wireOp",EDGE,"E4")]}),1.0]])],"derivedFrom":subQ0})])],"isStart":false});}
            var Q26;
            Q26=makeQuery(id+"F1.opExtrude","CAP_EDGE",EDGE,{"disambiguationData":[OSD([sQuery(id+"F0.wireOp",EDGE,"E8.1.3")])],"isStart":false});
            var Q27;
            Q27=makeQuery(id+"F1.opExtrude","CAP_EDGE",EDGE,{"disambiguationData":[OSD([sQuery(id+"F0.wireOp",EDGE,"E8.1.2")])],"isStart":false});
            var Q28;
            Q28=makeQuery(id+"F1.opExtrude","CAP_EDGE",EDGE,{"disambiguationData":[OSD([sQuery(id+"F0.wireOp",EDGE,"E8.1.1")])],"isStart":false});
            var Q29;
            Q29=makeQuery(id+"F1.opExtrude","CAP_EDGE",EDGE,{"disambiguationData":[OSD([sQuery(id+"F0.wireOp",EDGE,"E8.1.0")])],"isStart":false});
            var Q30;
            Q30=makeQuery(id+"F1.opExtrude","CAP_EDGE",EDGE,{"disambiguationData":[OSD([sQuery(id+"F0.wireOp",EDGE,"E8.1.9")])],"isStart":false});
            var Q31;
            {var subQ0=sQuery(id+"F0.wireOp",EDGE,"E8.1.11");Q31=makeQuery(id+"F1.opExtrude","CAP_EDGE",EDGE,{"disambiguationData":[OSD([subQ0]),TDD([makeQuery(id+"F0.imprint","IMPRINT",EDGE,{"disambiguationData":[TD([[makeQuery(id+"F0.imprint","INTERSECT",VERTEX,{"derivedFrom":[sQuery(id+"F0.wireOp",EDGE,"E8.1.9"),subQ0]}),1.0]])],"derivedFrom":subQ0})])],"isStart":false});}
            var Q32;
            Q32=makeQuery(id+"F1.opExtrude","CAP_EDGE",EDGE,{"disambiguationData":[OSD([sQuery(id+"F0.wireOp",EDGE,"E8.2.3")])],"isStart":false});
            var Q33;
            Q33=makeQuery(id+"F1.opExtrude","CAP_EDGE",EDGE,{"disambiguationData":[OSD([sQuery(id+"F0.wireOp",EDGE,"E8.2.2")])],"isStart":false});
            var Q34;
            Q34=makeQuery(id+"F1.opExtrude","CAP_EDGE",EDGE,{"disambiguationData":[OSD([sQuery(id+"F0.wireOp",EDGE,"E8.2.1")])],"isStart":false});
            var Q35;
            Q35=makeQuery(id+"F1.opExtrude","CAP_EDGE",EDGE,{"disambiguationData":[OSD([sQuery(id+"F0.wireOp",EDGE,"E8.2.0")])],"isStart":false});
            fillet(context, id + "F2", {"entities" : qUnion([Q0, Q1, Q2, Q3, Q4, Q5, Q6, Q7, Q8, Q9, Q10, Q11, Q12, Q13, Q14, Q15, Q16, Q17, Q18, Q19, Q20, Q21, Q22, Q23, Q24, Q25, Q26, Q27, Q28, Q29, Q30, Q31, Q32, Q33, Q34, Q35]), "radius" : 1.27 * mm, "tangentPropagation" : true, "allowEdgeOverflow" : false});
        }
        {
            var Q0;
            Q0=makeQuery(id+"F1.opExtrude","CAP_EDGE",EDGE,{"disambiguationData":[OSD([sQuery(id+"F0.wireOp",EDGE,"E7")])],"isStart":true});
            var Q1;
            Q1=makeQuery(id+"F1.opExtrude","CAP_EDGE",EDGE,{"disambiguationData":[OSD([sQuery(id+"F0.wireOp",EDGE,"E6.1")])],"isStart":true});
            var Q2;
            Q2=makeQuery(id+"F1.opExtrude","CAP_EDGE",EDGE,{"disambiguationData":[OSD([sQuery(id+"F0.wireOp",EDGE,"E6.2")])],"isStart":true});
            var Q3;
            {var subQ0=sQuery(id+"F0.wireOp",EDGE,"E9.32.5.0");Q3=makeQuery(id+"F1.opExtrude","CAP_EDGE",EDGE,{"disambiguationData":[OSD([subQ0]),TDD([makeQuery(id+"F0.imprint","IMPRINT",EDGE,{"disambiguationData":[TD([[makeQuery(id+"F0.imprint","INTERSECT",VERTEX,{"derivedFrom":[sQuery(id+"F0.wireOp",EDGE,"E9.26.5.0"),subQ0]}),1.0]])],"derivedFrom":subQ0})])],"isStart":true});}
            var Q4;
            Q4=makeQuery(id+"F1.opExtrude","CAP_EDGE",EDGE,{"disambiguationData":[OSD([sQuery(id+"F0.wireOp",EDGE,"E9.26.5.0")])],"isStart":true});
            var Q5;
            Q5=makeQuery(id+"F1.opExtrude","CAP_EDGE",EDGE,{"disambiguationData":[OSD([sQuery(id+"F0.wireOp",EDGE,"E9.2.5.0")])],"isStart":true});
            var Q6;
            Q6=makeQuery(id+"F1.opExtrude","CAP_EDGE",EDGE,{"disambiguationData":[OSD([sQuery(id+"F0.wireOp",EDGE,"E9.3.5.0")])],"isStart":true});
            var Q7;
            Q7=makeQuery(id+"F1.opExtrude","CAP_EDGE",EDGE,{"disambiguationData":[OSD([sQuery(id+"F0.wireOp",EDGE,"E9.6.5.0")])],"isStart":true});
            var Q8;
            Q8=makeQuery(id+"F1.opExtrude","CAP_EDGE",EDGE,{"disambiguationData":[OSD([sQuery(id+"F0.wireOp",EDGE,"E9.9.5.0")])],"isStart":true});
            var Q9;
            {var subQ0=sQuery(id+"F0.wireOp",EDGE,"E9.32.4.0");Q9=makeQuery(id+"F1.opExtrude","CAP_EDGE",EDGE,{"disambiguationData":[OSD([subQ0]),TDD([makeQuery(id+"F0.imprint","IMPRINT",EDGE,{"disambiguationData":[TD([[makeQuery(id+"F0.imprint","INTERSECT",VERTEX,{"derivedFrom":[sQuery(id+"F0.wireOp",EDGE,"E9.26.4.0"),subQ0]}),1.0]])],"derivedFrom":subQ0})])],"isStart":true});}
            var Q10;
            Q10=makeQuery(id+"F1.opExtrude","CAP_EDGE",EDGE,{"disambiguationData":[OSD([sQuery(id+"F0.wireOp",EDGE,"E9.26.4.0")])],"isStart":true});
            var Q11;
            Q11=makeQuery(id+"F1.opExtrude","CAP_EDGE",EDGE,{"disambiguationData":[OSD([sQuery(id+"F0.wireOp",EDGE,"E9.2.4.0")])],"isStart":true});
            var Q12;
            Q12=makeQuery(id+"F1.opExtrude","CAP_EDGE",EDGE,{"disambiguationData":[OSD([sQuery(id+"F0.wireOp",EDGE,"E9.3.4.0")])],"isStart":true});
            var Q13;
            Q13=makeQuery(id+"F1.opExtrude","CAP_EDGE",EDGE,{"disambiguationData":[OSD([sQuery(id+"F0.wireOp",EDGE,"E9.6.4.0")])],"isStart":true});
            var Q14;
            Q14=makeQuery(id+"F1.opExtrude","CAP_EDGE",EDGE,{"disambiguationData":[OSD([sQuery(id+"F0.wireOp",EDGE,"E9.9.4.0")])],"isStart":true});
            var Q15;
            {var subQ0=sQuery(id+"F0.wireOp",EDGE,"E9.32.3.0");Q15=makeQuery(id+"F1.opExtrude","CAP_EDGE",EDGE,{"disambiguationData":[OSD([subQ0]),TDD([makeQuery(id+"F0.imprint","IMPRINT",EDGE,{"disambiguationData":[TD([[makeQuery(id+"F0.imprint","INTERSECT",VERTEX,{"derivedFrom":[sQuery(id+"F0.wireOp",EDGE,"E9.26.3.0"),subQ0]}),1.0]])],"derivedFrom":subQ0})])],"isStart":true});}
            var Q16;
            Q16=makeQuery(id+"F1.opExtrude","CAP_EDGE",EDGE,{"disambiguationData":[OSD([sQuery(id+"F0.wireOp",EDGE,"E9.26.3.0")])],"isStart":true});
            var Q17;
            Q17=makeQuery(id+"F1.opExtrude","CAP_EDGE",EDGE,{"disambiguationData":[OSD([sQuery(id+"F0.wireOp",EDGE,"E9.2.3.0")])],"isStart":true});
            var Q18;
            Q18=makeQuery(id+"F1.opExtrude","CAP_EDGE",EDGE,{"disambiguationData":[OSD([sQuery(id+"F0.wireOp",EDGE,"E9.3.3.0")])],"isStart":true});
            var Q19;
            Q19=makeQuery(id+"F1.opExtrude","CAP_EDGE",EDGE,{"disambiguationData":[OSD([sQuery(id+"F0.wireOp",EDGE,"E9.6.3.0")])],"isStart":true});
            var Q20;
            Q20=makeQuery(id+"F1.opExtrude","CAP_EDGE",EDGE,{"disambiguationData":[OSD([sQuery(id+"F0.wireOp",EDGE,"E9.9.3.0")])],"isStart":true});
            var Q21;
            {var subQ0=sQuery(id+"F0.wireOp",EDGE,"E8.2.11");Q21=makeQuery(id+"F1.opExtrude","CAP_EDGE",EDGE,{"disambiguationData":[OSD([subQ0]),TDD([makeQuery(id+"F0.imprint","IMPRINT",EDGE,{"disambiguationData":[TD([[makeQuery(id+"F0.imprint","INTERSECT",VERTEX,{"derivedFrom":[sQuery(id+"F0.wireOp",EDGE,"E8.2.9"),subQ0]}),1.0]])],"derivedFrom":subQ0})])],"isStart":true});}
            var Q22;
            Q22=makeQuery(id+"F1.opExtrude","CAP_EDGE",EDGE,{"disambiguationData":[OSD([sQuery(id+"F0.wireOp",EDGE,"E8.2.9")])],"isStart":true});
            var Q23;
            Q23=makeQuery(id+"F1.opExtrude","CAP_EDGE",EDGE,{"disambiguationData":[OSD([sQuery(id+"F0.wireOp",EDGE,"E8.2.0")])],"isStart":true});
            var Q24;
            Q24=makeQuery(id+"F1.opExtrude","CAP_EDGE",EDGE,{"disambiguationData":[OSD([sQuery(id+"F0.wireOp",EDGE,"E8.2.1")])],"isStart":true});
            var Q25;
            Q25=makeQuery(id+"F1.opExtrude","CAP_EDGE",EDGE,{"disambiguationData":[OSD([sQuery(id+"F0.wireOp",EDGE,"E8.2.2")])],"isStart":true});
            var Q26;
            Q26=makeQuery(id+"F1.opExtrude","CAP_EDGE",EDGE,{"disambiguationData":[OSD([sQuery(id+"F0.wireOp",EDGE,"E8.2.3")])],"isStart":true});
            var Q27;
            {var subQ0=sQuery(id+"F0.wireOp",EDGE,"E8.1.11");Q27=makeQuery(id+"F1.opExtrude","CAP_EDGE",EDGE,{"disambiguationData":[OSD([subQ0]),TDD([makeQuery(id+"F0.imprint","IMPRINT",EDGE,{"disambiguationData":[TD([[makeQuery(id+"F0.imprint","INTERSECT",VERTEX,{"derivedFrom":[sQuery(id+"F0.wireOp",EDGE,"E8.1.9"),subQ0]}),1.0]])],"derivedFrom":subQ0})])],"isStart":true});}
            var Q28;
            Q28=makeQuery(id+"F1.opExtrude","CAP_EDGE",EDGE,{"disambiguationData":[OSD([sQuery(id+"F0.wireOp",EDGE,"E8.1.9")])],"isStart":true});
            var Q29;
            Q29=makeQuery(id+"F1.opExtrude","CAP_EDGE",EDGE,{"disambiguationData":[OSD([sQuery(id+"F0.wireOp",EDGE,"E8.1.0")])],"isStart":true});
            var Q30;
            Q30=makeQuery(id+"F1.opExtrude","CAP_EDGE",EDGE,{"disambiguationData":[OSD([sQuery(id+"F0.wireOp",EDGE,"E8.1.1")])],"isStart":true});
            var Q31;
            Q31=makeQuery(id+"F1.opExtrude","CAP_EDGE",EDGE,{"disambiguationData":[OSD([sQuery(id+"F0.wireOp",EDGE,"E8.1.2")])],"isStart":true});
            var Q32;
            Q32=makeQuery(id+"F1.opExtrude","CAP_EDGE",EDGE,{"disambiguationData":[OSD([sQuery(id+"F0.wireOp",EDGE,"E8.1.3")])],"isStart":true});
            var Q33;
            {var subQ0=sQuery(id+"F0.wireOp",EDGE,"E3");Q33=makeQuery(id+"F1.opExtrude","CAP_EDGE",EDGE,{"disambiguationData":[OSD([subQ0]),TDD([makeQuery(id+"F0.imprint","IMPRINT",EDGE,{"disambiguationData":[TD([[makeQuery(id+"F0.imprint","INTERSECT",VERTEX,{"derivedFrom":[subQ0,sQuery(id+"F0.wireOp",EDGE,"E4")]}),1.0]])],"derivedFrom":subQ0})])],"isStart":true});}
            var Q34;
            Q34=makeQuery(id+"F1.opExtrude","CAP_EDGE",EDGE,{"disambiguationData":[OSD([sQuery(id+"F0.wireOp",EDGE,"E4")])],"isStart":true});
            var Q35;
            Q35=makeQuery(id+"F1.opExtrude","CAP_EDGE",EDGE,{"disambiguationData":[OSD([sQuery(id+"F0.wireOp",EDGE,"E5")])],"isStart":true});
            fillet(context, id + "F3", {"entities" : qUnion([Q0, Q1, Q2, Q3, Q4, Q5, Q6, Q7, Q8, Q9, Q10, Q11, Q12, Q13, Q14, Q15, Q16, Q17, Q18, Q19, Q20, Q21, Q22, Q23, Q24, Q25, Q26, Q27, Q28, Q29, Q30, Q31, Q32, Q33, Q34, Q35]), "radius" : 1.27 * mm, "tangentPropagation" : true, "allowEdgeOverflow" : false});
        }
        {
            var Q0;
            Q0=makeQuery(id+"F1.opExtrude","CAP_EDGE",EDGE,{"disambiguationData":[OSD([sQuery(id+"F0.wireOp",EDGE,"E8.2.4")])],"isStart":false});
            var Q1;
            {var subQ0=sQuery(id+"F0.wireOp",EDGE,"E8.1.11");Q1=makeQuery(id+"F1.opExtrude","CAP_EDGE",EDGE,{"disambiguationData":[OSD([subQ0]),TDD([makeQuery(id+"F0.imprint","IMPRINT",EDGE,{"disambiguationData":[TD([[makeQuery(id+"F0.imprint","INTERSECT",VERTEX,{"derivedFrom":[subQ0,sQuery(id+"F0.wireOp",EDGE,"E8.2.4")]}),1.0]])],"derivedFrom":subQ0})])],"isStart":false});}
            var Q2;
            Q2=makeQuery(id+"F1.opExtrude","CAP_EDGE",EDGE,{"disambiguationData":[OSD([sQuery(id+"F0.wireOp",EDGE,"E8.2.18")])],"isStart":false});
            var Q3;
            {var subQ0=sQuery(id+"F0.wireOp",EDGE,"E8.2.11");Q3=makeQuery(id+"F1.opExtrude","CAP_EDGE",EDGE,{"disambiguationData":[OSD([subQ0]),TDD([makeQuery(id+"F0.imprint","IMPRINT",EDGE,{"disambiguationData":[TD([[makeQuery(id+"F0.imprint","INTERSECT",VERTEX,{"derivedFrom":[subQ0,sQuery(id+"F0.wireOp",EDGE,"E9.12.3.0")]}),1.0]])],"derivedFrom":subQ0})])],"isStart":false});}
            var Q4;
            Q4=makeQuery(id+"F1.opExtrude","CAP_EDGE",EDGE,{"disambiguationData":[OSD([sQuery(id+"F0.wireOp",EDGE,"E9.12.3.0")])],"isStart":false});
            var Q5;
            Q5=makeQuery(id+"F1.opExtrude","CAP_EDGE",EDGE,{"disambiguationData":[OSD([sQuery(id+"F0.wireOp",EDGE,"E9.51.3.0")])],"isStart":false});
            var Q6;
            Q6=makeQuery(id+"F1.opExtrude","CAP_EDGE",EDGE,{"disambiguationData":[OSD([sQuery(id+"F0.wireOp",EDGE,"E8.1.18")])],"isStart":false});
            var Q7;
            Q7=makeQuery(id+"F1.opExtrude","CAP_EDGE",EDGE,{"disambiguationData":[OSD([sQuery(id+"F0.wireOp",EDGE,"E8.1.4")])],"isStart":false});
            var Q8;
            {var subQ0=sQuery(id+"F0.wireOp",EDGE,"E3");Q8=makeQuery(id+"F1.opExtrude","CAP_EDGE",EDGE,{"disambiguationData":[OSD([subQ0]),TDD([makeQuery(id+"F0.imprint","IMPRINT",EDGE,{"disambiguationData":[TD([[makeQuery(id+"F0.imprint","INTERSECT",VERTEX,{"derivedFrom":[subQ0,sQuery(id+"F0.wireOp",EDGE,"E8.1.4")]}),1.0]])],"derivedFrom":subQ0})])],"isStart":false});}
            var Q9;
            Q9=makeQuery(id+"F1.opExtrude","CAP_EDGE",EDGE,{"disambiguationData":[OSD([sQuery(id+"F0.wireOp",EDGE,"E2")])],"isStart":false});
            var Q10;
            {var subQ0=sQuery(id+"F0.wireOp",EDGE,"E9.32.5.0");Q10=makeQuery(id+"F1.opExtrude","CAP_EDGE",EDGE,{"disambiguationData":[OSD([subQ0]),TDD([makeQuery(id+"F0.imprint","IMPRINT",EDGE,{"disambiguationData":[TD([[makeQuery(id+"F0.imprint","INTERSECT",VERTEX,{"derivedFrom":[sQuery(id+"F0.wireOp",EDGE,"E6.4"),subQ0]}),1.0]])],"derivedFrom":subQ0})])],"isStart":false});}
            var Q11;
            Q11=makeQuery(id+"F1.opExtrude","CAP_EDGE",EDGE,{"disambiguationData":[OSD([sQuery(id+"F0.wireOp",EDGE,"E6.4")])],"isStart":false});
            var Q12;
            {var subQ0=sQuery(id+"F0.wireOp",EDGE,"E9.32.4.0");Q12=makeQuery(id+"F1.opExtrude","CAP_EDGE",EDGE,{"disambiguationData":[OSD([subQ0]),TDD([makeQuery(id+"F0.imprint","IMPRINT",EDGE,{"disambiguationData":[TD([[makeQuery(id+"F0.imprint","INTERSECT",VERTEX,{"derivedFrom":[subQ0,sQuery(id+"F0.wireOp",EDGE,"E9.12.5.0")]}),1.0]])],"derivedFrom":subQ0})])],"isStart":false});}
            var Q13;
            {var subQ0=sQuery(id+"F0.wireOp",EDGE,"E9.32.3.0");Q13=makeQuery(id+"F1.opExtrude","CAP_EDGE",EDGE,{"disambiguationData":[OSD([subQ0]),TDD([makeQuery(id+"F0.imprint","IMPRINT",EDGE,{"disambiguationData":[TD([[makeQuery(id+"F0.imprint","INTERSECT",VERTEX,{"derivedFrom":[subQ0,sQuery(id+"F0.wireOp",EDGE,"E9.12.4.0")]}),1.0]])],"derivedFrom":subQ0})])],"isStart":false});}
            var Q14;
            Q14=makeQuery(id+"F1.opExtrude","CAP_EDGE",EDGE,{"disambiguationData":[OSD([sQuery(id+"F0.wireOp",EDGE,"E9.12.4.0")])],"isStart":false});
            var Q15;
            Q15=makeQuery(id+"F1.opExtrude","CAP_EDGE",EDGE,{"disambiguationData":[OSD([sQuery(id+"F0.wireOp",EDGE,"E9.51.4.0")])],"isStart":false});
            var Q16;
            Q16=makeQuery(id+"F1.opExtrude","CAP_EDGE",EDGE,{"disambiguationData":[OSD([sQuery(id+"F0.wireOp",EDGE,"E9.51.5.0")])],"isStart":false});
            var Q17;
            Q17=makeQuery(id+"F1.opExtrude","CAP_EDGE",EDGE,{"disambiguationData":[OSD([sQuery(id+"F0.wireOp",EDGE,"E9.12.5.0")])],"isStart":false});
            var Q18;
            {var subQ0=sQuery(id+"F0.wireOp",EDGE,"E9.32.4.0");Q18=makeQuery(id+"F1.opExtrude","CAP_EDGE",EDGE,{"disambiguationData":[OSD([subQ0]),TDD([makeQuery(id+"F0.imprint","IMPRINT",EDGE,{"disambiguationData":[TD([[makeQuery(id+"F0.imprint","INTERSECT",VERTEX,{"derivedFrom":[subQ0,sQuery(id+"F0.wireOp",EDGE,"E9.12.5.0")]}),1.0]])],"derivedFrom":subQ0})])],"isStart":true});}
            var Q19;
            Q19=makeQuery(id+"F1.opExtrude","CAP_EDGE",EDGE,{"disambiguationData":[OSD([sQuery(id+"F0.wireOp",EDGE,"E9.51.5.0")])],"isStart":true});
            var Q20;
            Q20=makeQuery(id+"F1.opExtrude","CAP_EDGE",EDGE,{"disambiguationData":[OSD([sQuery(id+"F0.wireOp",EDGE,"E9.12.5.0")])],"isStart":true});
            var Q21;
            Q21=makeQuery(id+"F1.opExtrude","CAP_EDGE",EDGE,{"disambiguationData":[OSD([sQuery(id+"F0.wireOp",EDGE,"E9.51.4.0")])],"isStart":true});
            var Q22;
            {var subQ0=sQuery(id+"F0.wireOp",EDGE,"E9.32.3.0");Q22=makeQuery(id+"F1.opExtrude","CAP_EDGE",EDGE,{"disambiguationData":[OSD([subQ0]),TDD([makeQuery(id+"F0.imprint","IMPRINT",EDGE,{"disambiguationData":[TD([[makeQuery(id+"F0.imprint","INTERSECT",VERTEX,{"derivedFrom":[subQ0,sQuery(id+"F0.wireOp",EDGE,"E9.12.4.0")]}),1.0]])],"derivedFrom":subQ0})])],"isStart":true});}
            var Q23;
            Q23=makeQuery(id+"F1.opExtrude","CAP_EDGE",EDGE,{"disambiguationData":[OSD([sQuery(id+"F0.wireOp",EDGE,"E9.12.4.0")])],"isStart":true});
            var Q24;
            Q24=makeQuery(id+"F1.opExtrude","CAP_EDGE",EDGE,{"disambiguationData":[OSD([sQuery(id+"F0.wireOp",EDGE,"E6.4")])],"isStart":true});
            var Q25;
            Q25=makeQuery(id+"F1.opExtrude","CAP_EDGE",EDGE,{"disambiguationData":[OSD([sQuery(id+"F0.wireOp",EDGE,"E2")])],"isStart":true});
            var Q26;
            {var subQ0=sQuery(id+"F0.wireOp",EDGE,"E9.32.5.0");Q26=makeQuery(id+"F1.opExtrude","CAP_EDGE",EDGE,{"disambiguationData":[OSD([subQ0]),TDD([makeQuery(id+"F0.imprint","IMPRINT",EDGE,{"disambiguationData":[TD([[makeQuery(id+"F0.imprint","INTERSECT",VERTEX,{"derivedFrom":[sQuery(id+"F0.wireOp",EDGE,"E6.4"),subQ0]}),1.0]])],"derivedFrom":subQ0})])],"isStart":true});}
            var Q27;
            {var subQ0=sQuery(id+"F0.wireOp",EDGE,"E3");Q27=makeQuery(id+"F1.opExtrude","CAP_EDGE",EDGE,{"disambiguationData":[OSD([subQ0]),TDD([makeQuery(id+"F0.imprint","IMPRINT",EDGE,{"disambiguationData":[TD([[makeQuery(id+"F0.imprint","INTERSECT",VERTEX,{"derivedFrom":[subQ0,sQuery(id+"F0.wireOp",EDGE,"E8.1.4")]}),1.0]])],"derivedFrom":subQ0})])],"isStart":true});}
            var Q28;
            Q28=makeQuery(id+"F1.opExtrude","CAP_EDGE",EDGE,{"disambiguationData":[OSD([sQuery(id+"F0.wireOp",EDGE,"E8.1.4")])],"isStart":true});
            var Q29;
            Q29=makeQuery(id+"F1.opExtrude","CAP_EDGE",EDGE,{"disambiguationData":[OSD([sQuery(id+"F0.wireOp",EDGE,"E8.1.18")])],"isStart":true});
            var Q30;
            {var subQ0=sQuery(id+"F0.wireOp",EDGE,"E8.1.11");Q30=makeQuery(id+"F1.opExtrude","CAP_EDGE",EDGE,{"disambiguationData":[OSD([subQ0]),TDD([makeQuery(id+"F0.imprint","IMPRINT",EDGE,{"disambiguationData":[TD([[makeQuery(id+"F0.imprint","INTERSECT",VERTEX,{"derivedFrom":[subQ0,sQuery(id+"F0.wireOp",EDGE,"E8.2.4")]}),1.0]])],"derivedFrom":subQ0})])],"isStart":true});}
            var Q31;
            Q31=makeQuery(id+"F1.opExtrude","CAP_EDGE",EDGE,{"disambiguationData":[OSD([sQuery(id+"F0.wireOp",EDGE,"E8.2.4")])],"isStart":true});
            var Q32;
            Q32=makeQuery(id+"F1.opExtrude","CAP_EDGE",EDGE,{"disambiguationData":[OSD([sQuery(id+"F0.wireOp",EDGE,"E8.2.18")])],"isStart":true});
            var Q33;
            {var subQ0=sQuery(id+"F0.wireOp",EDGE,"E8.2.11");Q33=makeQuery(id+"F1.opExtrude","CAP_EDGE",EDGE,{"disambiguationData":[OSD([subQ0]),TDD([makeQuery(id+"F0.imprint","IMPRINT",EDGE,{"disambiguationData":[TD([[makeQuery(id+"F0.imprint","INTERSECT",VERTEX,{"derivedFrom":[subQ0,sQuery(id+"F0.wireOp",EDGE,"E9.12.3.0")]}),1.0]])],"derivedFrom":subQ0})])],"isStart":true});}
            var Q34;
            Q34=makeQuery(id+"F1.opExtrude","CAP_EDGE",EDGE,{"disambiguationData":[OSD([sQuery(id+"F0.wireOp",EDGE,"E9.12.3.0")])],"isStart":true});
            var Q35;
            Q35=makeQuery(id+"F1.opExtrude","CAP_EDGE",EDGE,{"disambiguationData":[OSD([sQuery(id+"F0.wireOp",EDGE,"E9.51.3.0")])],"isStart":true});
            chamfer(context, id + "F4", {"entities" : qUnion([Q0, Q1, Q2, Q3, Q4, Q5, Q6, Q7, Q8, Q9, Q10, Q11, Q12, Q13, Q14, Q15, Q16, Q17, Q18, Q19, Q20, Q21, Q22, Q23, Q24, Q25, Q26, Q27, Q28, Q29, Q30, Q31, Q32, Q33, Q34, Q35]), "width" : 0.25 * mm, "tangentPropagation" : true});
        }
        {
            var Q0;
            Q0=makeQuery(id+"F1.opExtrude","SWEPT_EDGE",EDGE,{"disambiguationData":[OSD([sQuery(id+"F0.wireOp",EDGE,"E8.2.2"),sQuery(id+"F0.wireOp",EDGE,"E8.2.3")])]});
            var Q1;
            Q1=makeQuery(id+"F1.opExtrude","SWEPT_EDGE",EDGE,{"disambiguationData":[OSD([sQuery(id+"F0.wireOp",EDGE,"E8.2.1"),sQuery(id+"F0.wireOp",EDGE,"E8.2.2"),sQuery(id+"F0.wireOp",EDGE,"E8.2.14")])]});
            var Q2;
            Q2=makeQuery(id+"F1.opExtrude","SWEPT_EDGE",EDGE,{"disambiguationData":[OSD([sQuery(id+"F0.wireOp",EDGE,"E8.2.0"),sQuery(id+"F0.wireOp",EDGE,"E8.2.1")])]});
            var Q3;
            Q3=makeQuery(id+"F1.opExtrude","SWEPT_EDGE",EDGE,{"disambiguationData":[OSD([sQuery(id+"F0.wireOp",EDGE,"E8.2.0"),sQuery(id+"F0.wireOp",EDGE,"E8.2.9")])]});
            var Q4;
            Q4=makeQuery(id+"F1.opExtrude","SWEPT_EDGE",EDGE,{"disambiguationData":[OSD([sQuery(id+"F0.wireOp",EDGE,"E8.2.9"),sQuery(id+"F0.wireOp",EDGE,"E8.2.11")])]});
            var Q5;
            Q5=makeQuery(id+"F1.opExtrude","SWEPT_EDGE",EDGE,{"disambiguationData":[OSD([sQuery(id+"F0.wireOp",EDGE,"E9.6.3.0"),sQuery(id+"F0.wireOp",EDGE,"E9.9.3.0")])]});
            var Q6;
            Q6=makeQuery(id+"F1.opExtrude","SWEPT_EDGE",EDGE,{"disambiguationData":[OSD([sQuery(id+"F0.wireOp",EDGE,"E9.3.3.0"),sQuery(id+"F0.wireOp",EDGE,"E9.6.3.0"),sQuery(id+"F0.wireOp",EDGE,"E9.39.3.0")])]});
            var Q7;
            Q7=makeQuery(id+"F1.opExtrude","SWEPT_EDGE",EDGE,{"disambiguationData":[OSD([sQuery(id+"F0.wireOp",EDGE,"E9.2.3.0"),sQuery(id+"F0.wireOp",EDGE,"E9.3.3.0")])]});
            var Q8;
            Q8=makeQuery(id+"F1.opExtrude","SWEPT_EDGE",EDGE,{"disambiguationData":[OSD([sQuery(id+"F0.wireOp",EDGE,"E9.2.3.0"),sQuery(id+"F0.wireOp",EDGE,"E9.26.3.0")])]});
            var Q9;
            Q9=makeQuery(id+"F1.opExtrude","SWEPT_EDGE",EDGE,{"disambiguationData":[OSD([sQuery(id+"F0.wireOp",EDGE,"E9.6.4.0"),sQuery(id+"F0.wireOp",EDGE,"E9.9.4.0")])]});
            var Q10;
            Q10=makeQuery(id+"F1.opExtrude","SWEPT_EDGE",EDGE,{"disambiguationData":[OSD([sQuery(id+"F0.wireOp",EDGE,"E9.3.4.0"),sQuery(id+"F0.wireOp",EDGE,"E9.6.4.0"),sQuery(id+"F0.wireOp",EDGE,"E9.39.4.0")])]});
            var Q11;
            Q11=makeQuery(id+"F1.opExtrude","SWEPT_EDGE",EDGE,{"disambiguationData":[OSD([sQuery(id+"F0.wireOp",EDGE,"E9.2.4.0"),sQuery(id+"F0.wireOp",EDGE,"E9.3.4.0")])]});
            var Q12;
            Q12=makeQuery(id+"F1.opExtrude","SWEPT_EDGE",EDGE,{"disambiguationData":[OSD([sQuery(id+"F0.wireOp",EDGE,"E9.2.4.0"),sQuery(id+"F0.wireOp",EDGE,"E9.26.4.0")])]});
            var Q13;
            Q13=makeQuery(id+"F1.opExtrude","SWEPT_EDGE",EDGE,{"disambiguationData":[OSD([sQuery(id+"F0.wireOp",EDGE,"E9.26.4.0"),sQuery(id+"F0.wireOp",EDGE,"E9.32.4.0")])]});
            var Q14;
            Q14=makeQuery(id+"F1.opExtrude","SWEPT_EDGE",EDGE,{"disambiguationData":[OSD([sQuery(id+"F0.wireOp",EDGE,"E9.6.5.0"),sQuery(id+"F0.wireOp",EDGE,"E9.9.5.0")])]});
            var Q15;
            Q15=makeQuery(id+"F1.opExtrude","SWEPT_EDGE",EDGE,{"disambiguationData":[OSD([sQuery(id+"F0.wireOp",EDGE,"E9.3.5.0"),sQuery(id+"F0.wireOp",EDGE,"E9.6.5.0"),sQuery(id+"F0.wireOp",EDGE,"E9.39.5.0")])]});
            var Q16;
            Q16=makeQuery(id+"F1.opExtrude","SWEPT_EDGE",EDGE,{"disambiguationData":[OSD([sQuery(id+"F0.wireOp",EDGE,"E9.2.5.0"),sQuery(id+"F0.wireOp",EDGE,"E9.3.5.0")])]});
            var Q17;
            Q17=makeQuery(id+"F1.opExtrude","SWEPT_EDGE",EDGE,{"disambiguationData":[OSD([sQuery(id+"F0.wireOp",EDGE,"E9.2.5.0"),sQuery(id+"F0.wireOp",EDGE,"E9.26.5.0")])]});
            var Q18;
            Q18=makeQuery(id+"F1.opExtrude","SWEPT_EDGE",EDGE,{"disambiguationData":[OSD([sQuery(id+"F0.wireOp",EDGE,"E9.26.5.0"),sQuery(id+"F0.wireOp",EDGE,"E9.32.5.0")])]});
            var Q19;
            Q19=makeQuery(id+"F1.opExtrude","SWEPT_EDGE",EDGE,{"disambiguationData":[OSD([sQuery(id+"F0.wireOp",EDGE,"E6.1"),sQuery(id+"F0.wireOp",EDGE,"E6.2")])]});
            var Q20;
            Q20=makeQuery(id+"F1.opExtrude","SWEPT_EDGE",EDGE,{"disambiguationData":[OSD([sQuery(id+"F0.wireOp",EDGE,"E6.1"),sQuery(id+"F0.wireOp",EDGE,"E6.3"),sQuery(id+"F0.wireOp",EDGE,"E7")])]});
            var Q21;
            Q21=makeQuery(id+"F1.opExtrude","SWEPT_EDGE",EDGE,{"disambiguationData":[OSD([sQuery(id+"F0.wireOp",EDGE,"E5"),sQuery(id+"F0.wireOp",EDGE,"E7")])]});
            var Q22;
            Q22=makeQuery(id+"F1.opExtrude","SWEPT_EDGE",EDGE,{"disambiguationData":[OSD([sQuery(id+"F0.wireOp",EDGE,"E4"),sQuery(id+"F0.wireOp",EDGE,"E5")])]});
            var Q23;
            Q23=makeQuery(id+"F1.opExtrude","SWEPT_EDGE",EDGE,{"disambiguationData":[OSD([sQuery(id+"F0.wireOp",EDGE,"E8.1.2"),sQuery(id+"F0.wireOp",EDGE,"E8.1.3")])]});
            var Q24;
            Q24=makeQuery(id+"F1.opExtrude","SWEPT_EDGE",EDGE,{"disambiguationData":[OSD([sQuery(id+"F0.wireOp",EDGE,"E3"),sQuery(id+"F0.wireOp",EDGE,"E4")])]});
            var Q25;
            Q25=makeQuery(id+"F1.opExtrude","SWEPT_EDGE",EDGE,{"disambiguationData":[OSD([sQuery(id+"F0.wireOp",EDGE,"E9.26.3.0"),sQuery(id+"F0.wireOp",EDGE,"E9.32.3.0")])]});
            var Q26;
            Q26=makeQuery(id+"F1.opExtrude","SWEPT_EDGE",EDGE,{"disambiguationData":[OSD([sQuery(id+"F0.wireOp",EDGE,"E8.1.9"),sQuery(id+"F0.wireOp",EDGE,"E8.1.11")])]});
            var Q27;
            Q27=makeQuery(id+"F1.opExtrude","SWEPT_EDGE",EDGE,{"disambiguationData":[OSD([sQuery(id+"F0.wireOp",EDGE,"E8.1.0"),sQuery(id+"F0.wireOp",EDGE,"E8.1.9")])]});
            var Q28;
            Q28=makeQuery(id+"F1.opExtrude","SWEPT_EDGE",EDGE,{"disambiguationData":[OSD([sQuery(id+"F0.wireOp",EDGE,"E8.1.0"),sQuery(id+"F0.wireOp",EDGE,"E8.1.1")])]});
            var Q29;
            Q29=makeQuery(id+"F1.opExtrude","SWEPT_EDGE",EDGE,{"disambiguationData":[OSD([sQuery(id+"F0.wireOp",EDGE,"E8.1.1"),sQuery(id+"F0.wireOp",EDGE,"E8.1.2"),sQuery(id+"F0.wireOp",EDGE,"E8.1.14")])]});
            fillet(context, id + "F5", {"entities" : qUnion([Q0, Q1, Q2, Q3, Q4, Q5, Q6, Q7, Q8, Q9, Q10, Q11, Q12, Q13, Q14, Q15, Q16, Q17, Q18, Q19, Q20, Q21, Q22, Q23, Q24, Q25, Q26, Q27, Q28, Q29]), "radius" : 6.35 * mm, "tangentPropagation" : true, "allowEdgeOverflow" : false});
        }
        {
            var Q0;
            Q0=makeQuery(id+"F1.opExtrude","SWEPT_EDGE",EDGE,{"disambiguationData":[OSD([sQuery(id+"F0.wireOp",EDGE,"E11"),sQuery(id+"F0.wireOp",EDGE,"E14")])]});
            var Q1;
            Q1=makeQuery(id+"F1.opExtrude","SWEPT_EDGE",EDGE,{"disambiguationData":[OSD([sQuery(id+"F0.wireOp",EDGE,"E15.1.2"),sQuery(id+"F0.wireOp",EDGE,"E15.1.3")])]});
            var Q2;
            Q2=makeQuery(id+"F1.opExtrude","SWEPT_EDGE",EDGE,{"disambiguationData":[OSD([sQuery(id+"F0.wireOp",EDGE,"E15.2.2"),sQuery(id+"F0.wireOp",EDGE,"E15.2.3")])]});
            var Q3;
            Q3=makeQuery(id+"F1.opExtrude","SWEPT_EDGE",EDGE,{"disambiguationData":[OSD([sQuery(id+"F0.wireOp",EDGE,"E16.6.3.0"),sQuery(id+"F0.wireOp",EDGE,"E16.9.3.0")])]});
            var Q4;
            Q4=makeQuery(id+"F1.opExtrude","SWEPT_EDGE",EDGE,{"disambiguationData":[OSD([sQuery(id+"F0.wireOp",EDGE,"E16.6.4.0"),sQuery(id+"F0.wireOp",EDGE,"E16.9.4.0")])]});
            var Q5;
            Q5=makeQuery(id+"F1.opExtrude","SWEPT_EDGE",EDGE,{"disambiguationData":[OSD([sQuery(id+"F0.wireOp",EDGE,"E16.6.5.0"),sQuery(id+"F0.wireOp",EDGE,"E16.9.5.0")])]});
            chamfer(context, id + "F6", {"entities" : qUnion([Q0, Q1, Q2, Q3, Q4, Q5]), "width" : 4.44 * mm, "tangentPropagation" : true});
        }
        {
            var Q0;
            Q0=makeQuery(id+"F1.opExtrude","SWEPT_EDGE",EDGE,{"disambiguationData":[OSD([sQuery(id+"F0.wireOp",EDGE,"E19.0"),sQuery(id+"F0.wireOp",EDGE,"E19.1")])]});
            var Q1;
            Q1=makeQuery(id+"F1.opExtrude","SWEPT_EDGE",EDGE,{"disambiguationData":[OSD([sQuery(id+"F0.wireOp",EDGE,"E17"),sQuery(id+"F0.wireOp",EDGE,"E18")])]});
            var Q2;
            Q2=makeQuery(id+"F1.opExtrude","SWEPT_EDGE",EDGE,{"disambiguationData":[OSD([sQuery(id+"F0.wireOp",EDGE,"E23.3.5.0"),sQuery(id+"F0.wireOp",EDGE,"E23.6.5.0")])]});
            var Q3;
            Q3=makeQuery(id+"F1.opExtrude","SWEPT_EDGE",EDGE,{"disambiguationData":[OSD([sQuery(id+"F0.wireOp",EDGE,"E23.3.4.0"),sQuery(id+"F0.wireOp",EDGE,"E23.6.4.0")])]});
            var Q4;
            Q4=makeQuery(id+"F1.opExtrude","SWEPT_EDGE",EDGE,{"disambiguationData":[OSD([sQuery(id+"F0.wireOp",EDGE,"E22.1.1"),sQuery(id+"F0.wireOp",EDGE,"E22.1.2")])]});
            var Q5;
            Q5=makeQuery(id+"F1.opExtrude","SWEPT_EDGE",EDGE,{"disambiguationData":[OSD([sQuery(id+"F0.wireOp",EDGE,"E22.2.1"),sQuery(id+"F0.wireOp",EDGE,"E22.2.2")])]});
            var Q6;
            Q6=makeQuery(id+"F1.opExtrude","SWEPT_EDGE",EDGE,{"disambiguationData":[OSD([sQuery(id+"F0.wireOp",EDGE,"E23.3.3.0"),sQuery(id+"F0.wireOp",EDGE,"E23.6.3.0")])]});
            var Q7;
            Q7=makeQuery(id+"F1.opExtrude","SWEPT_EDGE",EDGE,{"disambiguationData":[OSD([sQuery(id+"F0.wireOp",EDGE,"E6.0"),sQuery(id+"F0.wireOp",EDGE,"E6.5")])]});
            var Q8;
            Q8=makeQuery(id+"F1.opExtrude","SWEPT_EDGE",EDGE,{"disambiguationData":[OSD([sQuery(id+"F0.wireOp",EDGE,"E9.15.5.0"),sQuery(id+"F0.wireOp",EDGE,"E9.18.5.0")])]});
            var Q9;
            Q9=makeQuery(id+"F1.opExtrude","SWEPT_EDGE",EDGE,{"disambiguationData":[OSD([sQuery(id+"F0.wireOp",EDGE,"E9.15.4.0"),sQuery(id+"F0.wireOp",EDGE,"E9.18.4.0")])]});
            var Q10;
            Q10=makeQuery(id+"F1.opExtrude","SWEPT_EDGE",EDGE,{"disambiguationData":[OSD([sQuery(id+"F0.wireOp",EDGE,"E9.15.3.0"),sQuery(id+"F0.wireOp",EDGE,"E9.18.3.0")])]});
            var Q11;
            Q11=makeQuery(id+"F1.opExtrude","SWEPT_EDGE",EDGE,{"disambiguationData":[OSD([sQuery(id+"F0.wireOp",EDGE,"E8.2.5"),sQuery(id+"F0.wireOp",EDGE,"E8.2.6")])]});
            fillet(context, id + "F7", {"entities" : qUnion([Q0, Q1, Q2, Q3, Q4, Q5, Q6, Q7, Q8, Q9, Q10, Q11]), "radius" : 5.08 * mm, "tangentPropagation" : true, "allowEdgeOverflow" : false});
        }
    });
